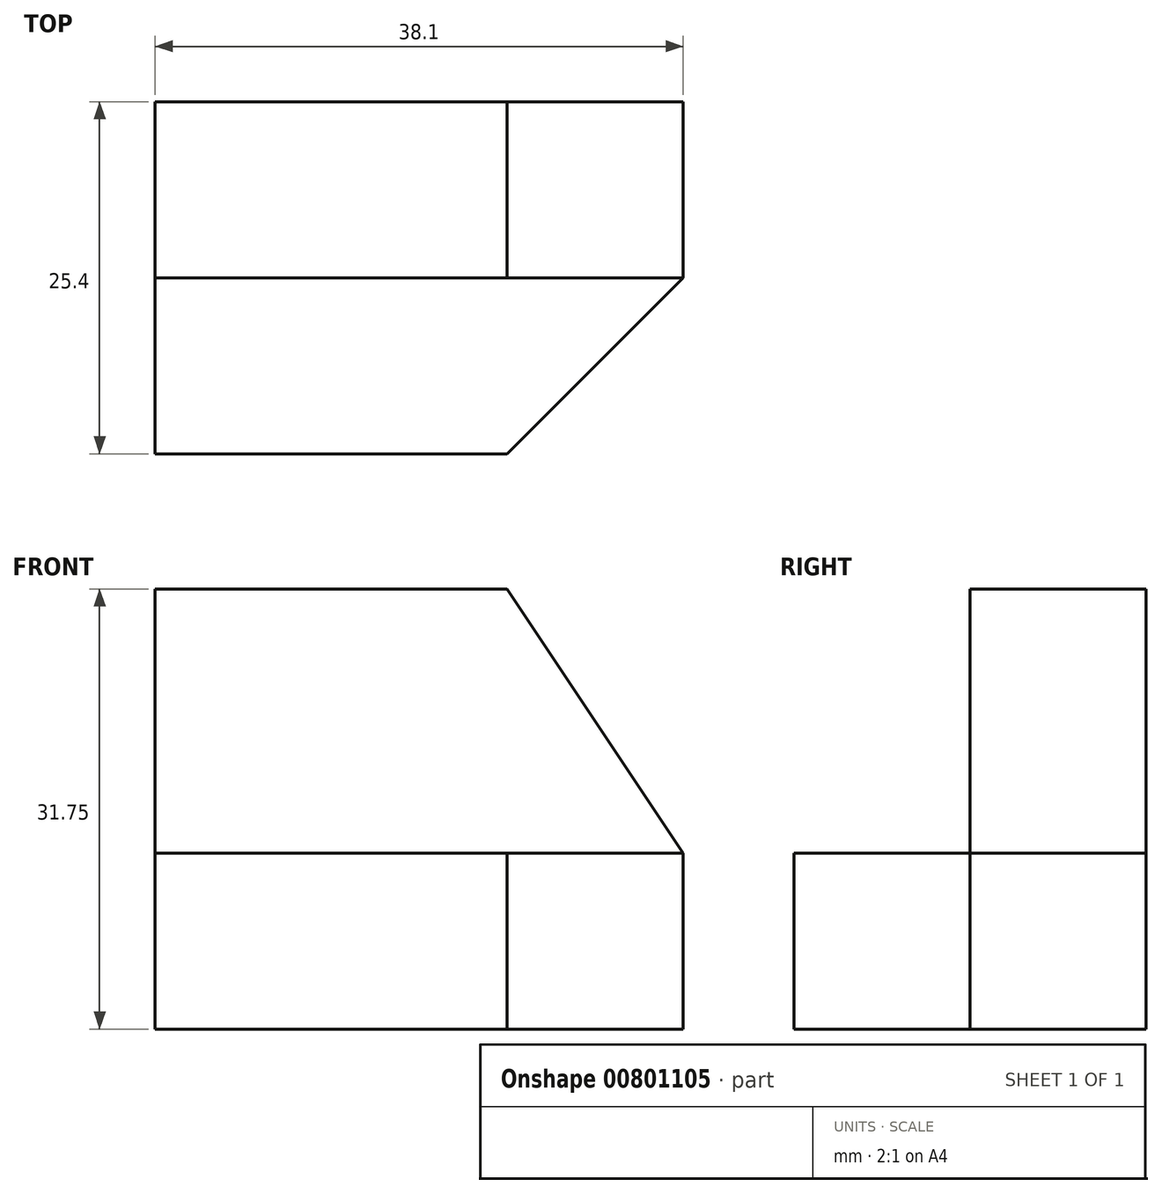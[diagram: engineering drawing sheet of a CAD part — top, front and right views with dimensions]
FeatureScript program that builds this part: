
annotation { "Feature Type Name" : "Feature", "Feature Type Description" : "" }
export const myFeature = defineFeature(function(context is Context, id is Id, definition is map)
    precondition{}
    {
        {
            var Q0;
            Q0=qCreatedBy(makeId("Right.planeOp"),FACE);
            var sketch = newSketch(context, id + "F0", { "sketchPlane" : qUnion([Q0])});
            skLineSegment(sketch, "E0", {"start": v(0, -1.5) * mm, "end": v(0, 11.2) * mm});
            skLineSegment(sketch, "E1", {"start": v(0, 11.2) * mm, "end": v(12.7, 11.2) * mm});
            skLineSegment(sketch, "E2", {"start": v(12.7, 11.2) * mm, "end": v(12.7, 30.24) * mm});
            skLineSegment(sketch, "E3", {"start": v(12.7, 30.24) * mm, "end": v(25.4, 30.24) * mm});
            skLineSegment(sketch, "E4", {"start": v(25.4, 30.24) * mm, "end": v(25.4, -1.5) * mm});
            skLineSegment(sketch, "E5", {"start": v(25.4, -1.5) * mm, "end": v(0, -1.5) * mm});
            skSolve(sketch);
        }
        {
            var Q0;
            Q0 = qSketchRegion(id + "F0", true);
            extrude(context, id + "F1", {"entities" : qUnion([Q0]), "depth" : 38.1 * mm, "offsetDistance" : 25.4 * mm});
        }
        {
            var Q0;
            Q0=makeQuery(id+"F1.opExtrude","SWEPT_FACE",FACE,{"disambiguationData":[OSD([sQuery(id+"F0.wireOp",EDGE,"E1")])]});
            var sketch = newSketch(context, id + "F2", { "sketchPlane" : qUnion([Q0])});
            skLineSegment(sketch, "E6", {"start": v(0, 0) * mm, "end": v(25.4, 0) * mm, "construction": true});
            skLineSegment(sketch, "E7", {"start": v(25.4, 0) * mm, "end": v(38.1, 12.7) * mm});
            skSolve(sketch);
        }
        {
            var Q0;
            Q0 = qSketchRegion(id + "F2", true);
            var Q1;
            {var subQ0=sQuery(id+"F2.wireOp",EDGE,"E7");Q1=makeQuery(id+"F2.imprint","IMPRINT",FACE,{"disambiguationData":[TD([[makeQuery(id+"F2.imprint","IMPRINT",EDGE,{"derivedFrom":subQ0}),-1.0]])]});}
            extrude(context, id + "F3", {"entities" : qUnion([Q0, Q1]), "operationType" : NewBodyOperationType.REMOVE, "oppositeDirection" : true, "depth" : 15.24 * mm, "offsetDistance" : 25.4 * mm});
        }
        {
            var Q0;
            {var subQ0=sQuery(id+"F2.wireOp",EDGE,"E7");Q0=makeQuery(id+"F2.imprint","IMPRINT",FACE,{"disambiguationData":[TD([[makeQuery(id+"F2.imprint","IMPRINT",EDGE,{"derivedFrom":subQ0}),-1.0]])]});}
            extrude(context, id + "F4", {"entities" : qUnion([Q0]), "operationType" : NewBodyOperationType.REMOVE, "oppositeDirection" : true, "depth" : 25.4 * mm, "offsetDistance" : 25.4 * mm});
        }
        {
            var Q0;
            Q0=makeQuery(id+"F1.opExtrude","SWEPT_FACE",FACE,{"disambiguationData":[OSD([sQuery(id+"F0.wireOp",EDGE,"E2")])]});
            var sketch = newSketch(context, id + "F5", { "sketchPlane" : qUnion([Q0])});
            skLineSegment(sketch, "E8", {"start": v(0, 30.24) * mm, "end": v(25.4, 30.24) * mm});
            skLineSegment(sketch, "E9", {"start": v(25.4, 30.24) * mm, "end": v(38.1, 11.2) * mm});
            skSolve(sketch);
        }
        {
            var Q0;
            Q0 = qSketchRegion(id + "F5", true);
            var Q1;
            {var subQ0=sQuery(id+"F5.wireOp",EDGE,"E9");Q1=makeQuery(id+"F5.imprint","IMPRINT",FACE,{"disambiguationData":[TD([[makeQuery(id+"F5.imprint","IMPRINT",EDGE,{"derivedFrom":subQ0}),1.0]])]});}
            extrude(context, id + "F6", {"entities" : qUnion([Q0, Q1]), "operationType" : NewBodyOperationType.REMOVE, "oppositeDirection" : true, "depth" : 25.4 * mm, "offsetDistance" : 25.4 * mm});
        }
    });
